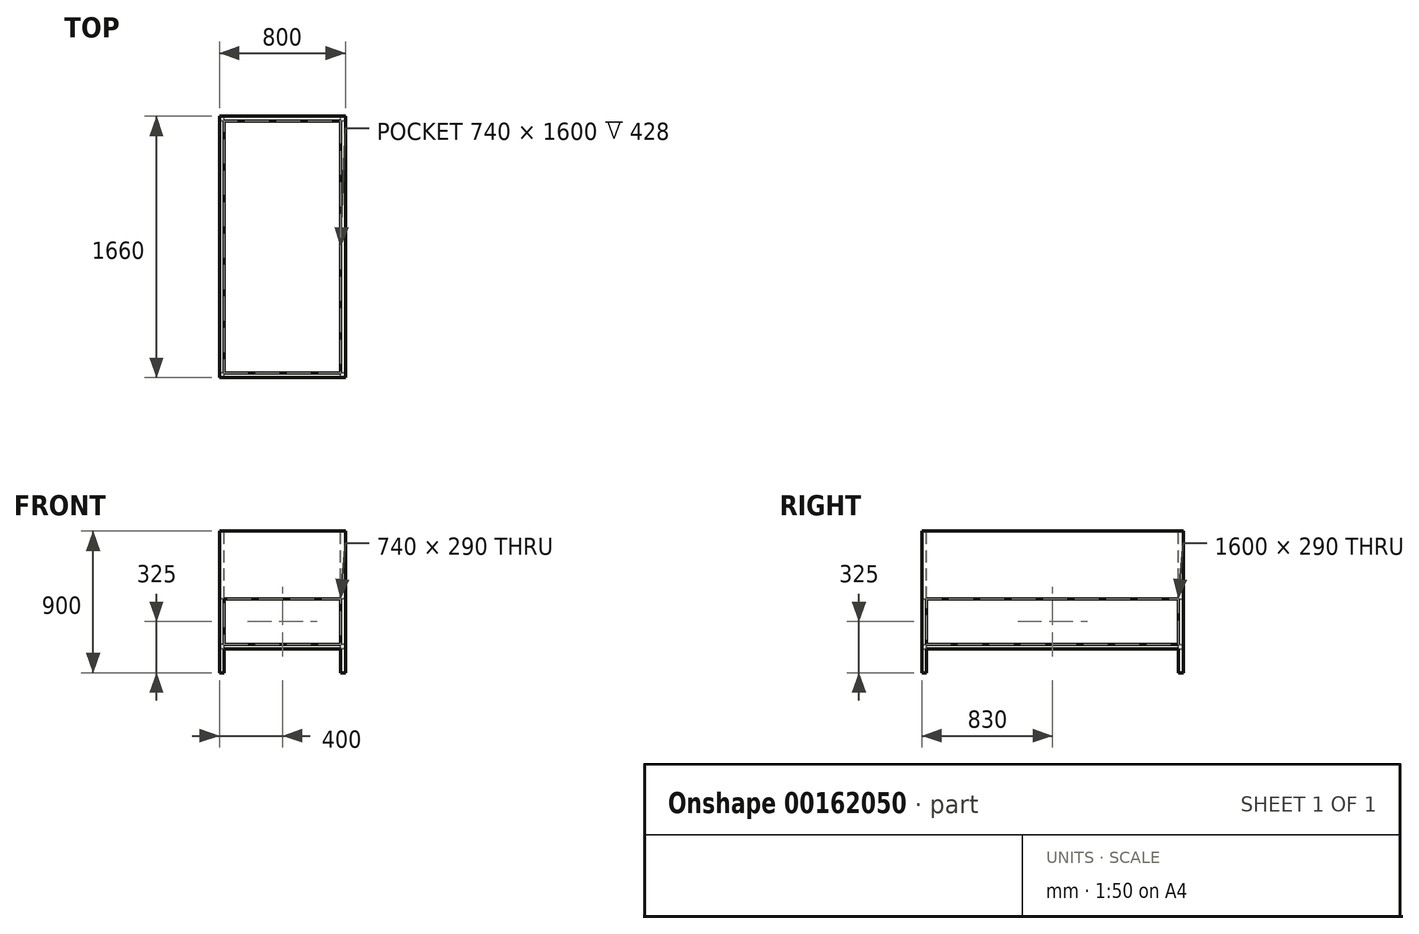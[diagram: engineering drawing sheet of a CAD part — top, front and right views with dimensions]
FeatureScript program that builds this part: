
annotation { "Feature Type Name" : "Feature", "Feature Type Description" : "" }
export const myFeature = defineFeature(function(context is Context, id is Id, definition is map)
    precondition{}
    {
        {
            var Q0;
            Q0=qCreatedBy(makeId("Right.planeOp"),FACE);
            var sketch = newSketch(context, id + "F0", { "sketchPlane" : qUnion([Q0])});
            skLineSegment(sketch, "E0", {"start": v(0, 0) * mm, "end": v(0, 500) * mm});
            skLineSegment(sketch, "E1", {"start": v(0, 500) * mm, "end": v(1660, 500) * mm});
            skLineSegment(sketch, "E2", {"start": v(1660, 500) * mm, "end": v(1660, 0) * mm});
            skLineSegment(sketch, "E3", {"start": v(1660, 0) * mm, "end": v(1630, 0) * mm});
            skLineSegment(sketch, "E4", {"start": v(1630, 0) * mm, "end": v(1630, 150) * mm});
            skLineSegment(sketch, "E5", {"start": v(1630, 150) * mm, "end": v(30, 150) * mm});
            skLineSegment(sketch, "E6", {"start": v(30, 150) * mm, "end": v(30, 0) * mm});
            skLineSegment(sketch, "E7", {"start": v(30, 0) * mm, "end": v(0, 0) * mm});
            skLineSegment(sketch, "E8.bottom", {"start": v(30, 470) * mm, "end": v(1630, 470) * mm});
            skLineSegment(sketch, "E8.top", {"start": v(30, 180) * mm, "end": v(1630, 180) * mm});
            skLineSegment(sketch, "E8.left", {"start": v(30, 470) * mm, "end": v(30, 180) * mm});
            skLineSegment(sketch, "E8.right", {"start": v(1630, 470) * mm, "end": v(1630, 180) * mm});
            skSolve(sketch);
        }
        {
            var Q0;
            Q0 = qSketchRegion(id + "F0", true);
            extrude(context, id + "F1", {"entities" : qUnion([Q0]), "depth" : 800 * mm});
        }
        {
            var Q0;
            Q0=makeQuery(id+"F1.opExtrude","SWEPT_FACE",FACE,{"disambiguationData":[OSD([sQuery(id+"F0.wireOp",EDGE,"E1")])]});
            var sketch = newSketch(context, id + "F2", { "sketchPlane" : qUnion([Q0])});
            skLineSegment(sketch, "E9.bottom", {"start": v(770, 30) * mm, "end": v(30, 30) * mm});
            skLineSegment(sketch, "E9.top", {"start": v(770, 1630) * mm, "end": v(30, 1630) * mm});
            skLineSegment(sketch, "E9.left", {"start": v(770, 30) * mm, "end": v(770, 1630) * mm});
            skLineSegment(sketch, "E9.right", {"start": v(30, 30) * mm, "end": v(30, 1630) * mm});
            skLineSegment(sketch, "E10.top", {"start": v(0, 1630) * mm, "end": v(385, 1630) * mm});
            skSolve(sketch);
        }
        {
            var Q0;
            Q0 = qSketchRegion(id + "F2", true);
            extrude(context, id + "F3", {"entities" : qUnion([Q0]), "operationType" : NewBodyOperationType.REMOVE, "endBound" : BoundingType.THROUGH_ALL, "oppositeDirection" : true, "depth" : 25 * mm});
        }
        {
            var Q0;
            Q0=makeQuery(id+"F1.opExtrude","SWEPT_FACE",FACE,{"disambiguationData":[OSD([sQuery(id+"F0.wireOp",EDGE,"E2")])]});
            var sketch = newSketch(context, id + "F4", { "sketchPlane" : qUnion([Q0])});
            skLineSegment(sketch, "E11.bottom", {"start": v(-770, 0) * mm, "end": v(-30, 0) * mm});
            skLineSegment(sketch, "E11.top", {"start": v(-770, 150) * mm, "end": v(-30, 150) * mm});
            skLineSegment(sketch, "E11.left", {"start": v(-770, 0) * mm, "end": v(-770, 150) * mm});
            skLineSegment(sketch, "E11.right", {"start": v(-30, 0) * mm, "end": v(-30, 150) * mm});
            skLineSegment(sketch, "E12.bottom", {"start": v(-770, 470) * mm, "end": v(-30, 470) * mm});
            skLineSegment(sketch, "E12.top", {"start": v(-770, 180) * mm, "end": v(-30, 180) * mm});
            skLineSegment(sketch, "E12.left", {"start": v(-770, 470) * mm, "end": v(-770, 180) * mm});
            skLineSegment(sketch, "E12.right", {"start": v(-30, 470) * mm, "end": v(-30, 180) * mm});
            skSolve(sketch);
        }
        {
            var Q0;
            Q0 = qSketchRegion(id + "F4", true);
            extrude(context, id + "F5", {"entities" : qUnion([Q0]), "operationType" : NewBodyOperationType.REMOVE, "endBound" : BoundingType.THROUGH_ALL, "oppositeDirection" : true, "depth" : 25 * mm});
        }
        {
            var Q0;
            Q0=makeQuery(id+"F1.opExtrude","SWEPT_FACE",FACE,{"disambiguationData":[OSD([sQuery(id+"F0.wireOp",EDGE,"E1")])]});
            var sketch = newSketch(context, id + "F6", { "sketchPlane" : qUnion([Q0])});
            skLineSegment(sketch, "E13.bottom", {"start": v(800, 1660) * mm, "end": v(0, 1660) * mm});
            skLineSegment(sketch, "E13.top", {"start": v(800, 0) * mm, "end": v(0, 0) * mm});
            skLineSegment(sketch, "E13.left", {"start": v(800, 1660) * mm, "end": v(800, 0) * mm});
            skLineSegment(sketch, "E13.right", {"start": v(0, 1660) * mm, "end": v(0, 0) * mm});
            skLineSegment(sketch, "E14.bottom", {"start": v(770, 30) * mm, "end": v(30, 30) * mm});
            skLineSegment(sketch, "E14.top", {"start": v(770, 1630) * mm, "end": v(30, 1630) * mm});
            skLineSegment(sketch, "E14.left", {"start": v(770, 30) * mm, "end": v(770, 1630) * mm});
            skLineSegment(sketch, "E14.right", {"start": v(30, 30) * mm, "end": v(30, 1630) * mm});
            skSolve(sketch);
        }
        {
            var Q0;
            Q0 = qSketchRegion(id + "F6", true);
            extrude(context, id + "F7", {"entities" : qUnion([Q0]), "operationType" : NewBodyOperationType.ADD, "depth" : 400 * mm});
        }
        {
            var Q0;
            Q0=makeQuery(id+"F5.boolean.opBoolean","COPY",FACE,{"disambiguationData":[TD([makeQuery(id+"F1.opExtrude","SWEPT_FACE",FACE,{"disambiguationData":[OSD([sQuery(id+"F0.wireOp",EDGE,"E2")])]})])],"derivedFrom":makeQuery(id+"F5.opExtrude","SWEPT_FACE",FACE,{"disambiguationData":[OSD([sQuery(id+"F4.wireOp",EDGE,"E12.bottom")])]})});
            var sketch = newSketch(context, id + "F8", { "sketchPlane" : qUnion([Q0])});
            skLineSegment(sketch, "E15.bottom", {"start": v(770, -1660) * mm, "end": v(0, -1660) * mm});
            skLineSegment(sketch, "E15.top", {"start": v(770, 0) * mm, "end": v(0, 0) * mm});
            skLineSegment(sketch, "E15.left", {"start": v(770, -1660) * mm, "end": v(770, 0) * mm});
            skLineSegment(sketch, "E15.right", {"start": v(0, -1660) * mm, "end": v(0, 0) * mm});
            skSolve(sketch);
        }
        {
            var Q0;
            Q0 = qSketchRegion(id + "F8", true);
            extrude(context, id + "F9", {"entities" : qUnion([Q0]), "operationType" : NewBodyOperationType.ADD, "oppositeDirection" : true, "depth" : 2 * mm});
        }
    });
